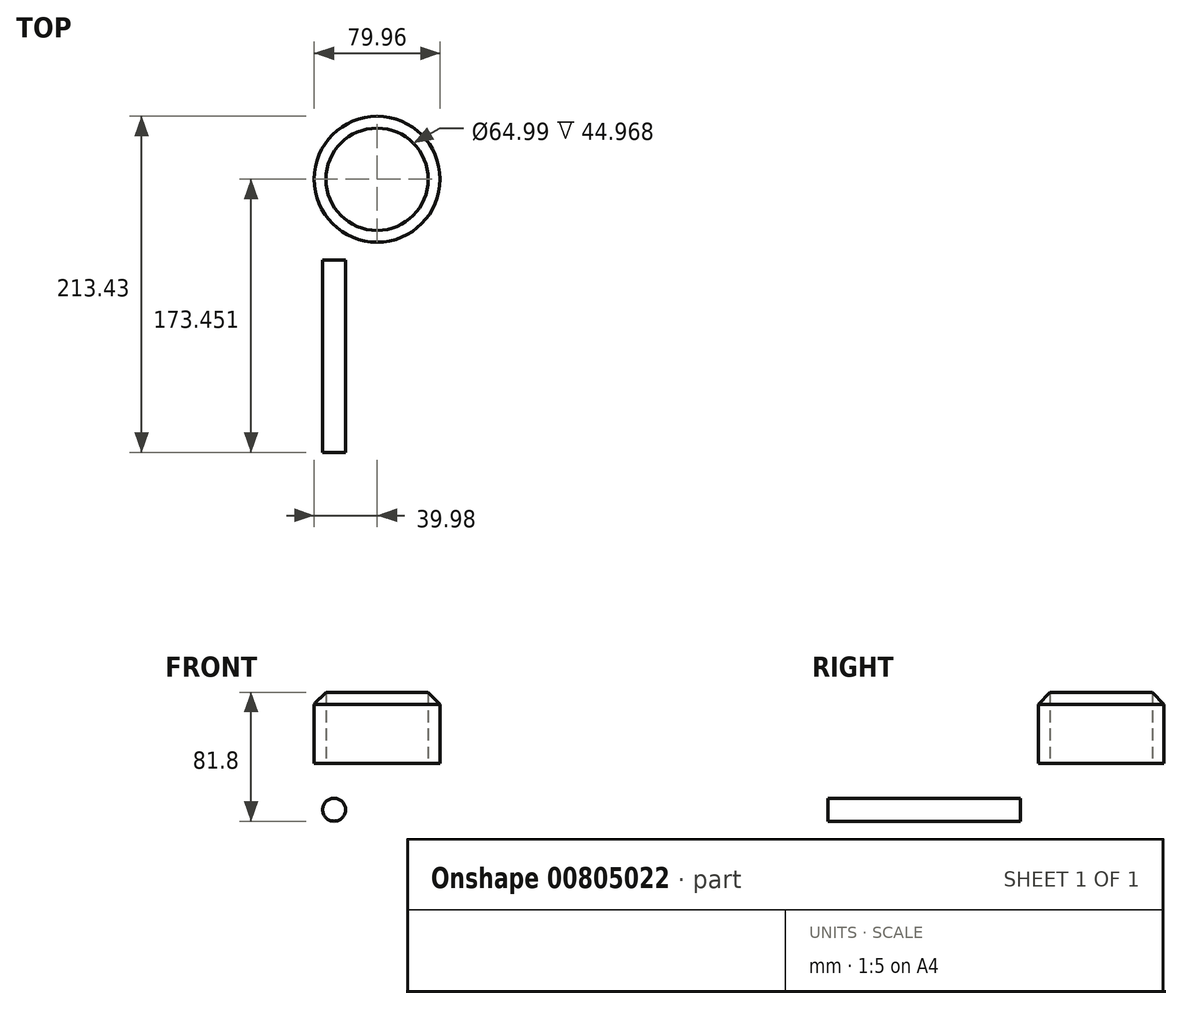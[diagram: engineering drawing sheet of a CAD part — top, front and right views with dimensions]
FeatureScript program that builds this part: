
annotation { "Feature Type Name" : "Feature", "Feature Type Description" : "" }
export const myFeature = defineFeature(function(context is Context, id is Id, definition is map)
    precondition{}
    {
        {
            var Q0;
            Q0=qCreatedBy(makeId("Top.planeOp"),FACE);
            var sketch = newSketch(context, id + "F0", { "sketchPlane" : qUnion([Q0])});
            skCircle(sketch, "E0", {"center": v(0, 51.21) * mm, "radius": 32.5 * mm});
            skCircle(sketch, "E1", {"center": v(0, 51.21) * mm, "radius": 39.98 * mm});
            skSolve(sketch);
        }
        {
            var Q0;
            Q0 = qSketchRegion(id + "F0", true);
            extrude(context, id + "F1", {"entities" : qUnion([Q0]), "depth" : 45.1 * mm, "offsetDistance" : 25.4 * mm});
        }
        {
            var Q0;
            Q0=makeQuery(id+"F1.opExtrude","CAP_EDGE",EDGE,{"disambiguationData":[OSD([sQuery(id+"F0.wireOp",EDGE,"E1")])],"isStart":false});
            chamfer(context, id + "F2", {"entities" : qUnion([Q0]), "width" : 7.62 * mm, "tangentPropagation" : true});
        }
        {
            var Q0;
            Q0=qCreatedBy(makeId("Front.planeOp"),FACE);
            var sketch = newSketch(context, id + "F3", { "sketchPlane" : qUnion([Q0])});
            skCircle(sketch, "E2", {"center": v(-27.32, -29.55) * mm, "radius": 7.27 * mm});
            skSolve(sketch);
        }
        {
            var Q0;
            Q0 = qSketchRegion(id + "F3", true);
            extrude(context, id + "F4", {"entities" : qUnion([Q0]), "depth" : 122.24 * mm, "offsetDistance" : 25.4 * mm});
        }
    });
